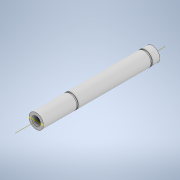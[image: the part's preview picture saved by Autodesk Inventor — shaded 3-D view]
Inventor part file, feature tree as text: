
AUTODESK INVENTOR PART (.ipt)
format: ipt  version: 2022 (Build 260153000, 153)  size: 138,752 bytes
history: native  units: in
note: dims shown in document units (in); Inventor stores cm internally (conversion verified against a paired STEP export)
features: sketch x5, extrude x2, revolve x2, other x1, projected_geometry x1
ambient origin geometry x8: Origin, YZ Plane, XZ Plane, XY Plane, X Axis, Y Axis, Z Axis, Center Point
bodies: Solid1 (feature_tree)
feature tree (11):
  extrude  "Extrusion1"  Depth=3.1496in TaperAngle=0.0deg
  sketch  "Sketch3"  dims[d3=0.1969in d4=0.0394in]
  other  "Work Axis1"
  revolve  "Revolution1"  [1 undecoded]
  revolve  "Revolution2"  Angle=90.0deg
  extrude  "Extrusion2"  Depth=0.0394in
  sketch  "Sketch2"  dims[d0=0.3937in d1=3.1496in d2=0.0in]
  projected_geometry  "Projected Loop1"
  sketch  "Sketch4"  dims[d5=0.0157in d6=90.0deg]
  sketch  "Sketch5"  dims[d7=1.9685in d8=0.0394in]
  sketch  "Sketch7"  dims[d9=0.0157in d10=90.0deg d11=0.2362in d12=0.3937in d13=0.0in]
note: 1 required parameter value undecoded (feature->parameter linkage not recoverable at this tier; creation-order binding heuristic only, values carry confidence <= 0.55)
